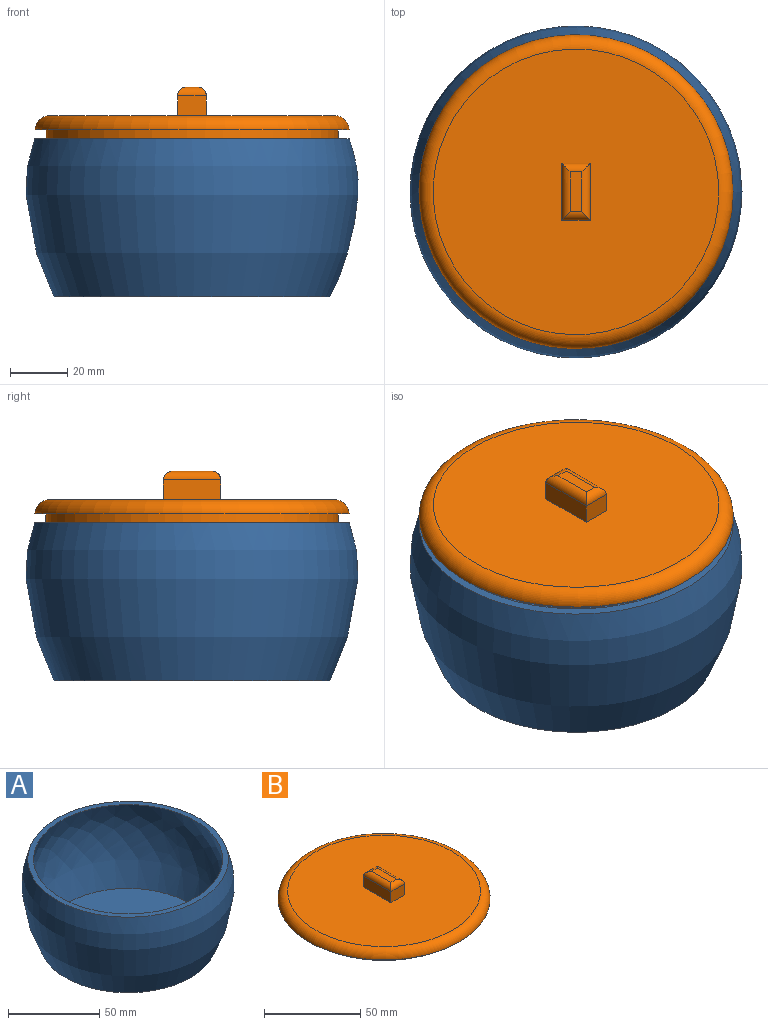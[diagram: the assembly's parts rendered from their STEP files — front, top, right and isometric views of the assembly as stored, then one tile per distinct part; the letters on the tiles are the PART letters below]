
ASSEMBLY  parts=2 mates=1
PART A: 5 faces, bbox 116.5x116.5x55.5 mm
  f0: plane 96.72x96.72mm, normal (0,0,-1), area 7347.7mm2, adj f1
  f1: revolved ~116.54x116.54mm, area 20018.4mm2, adj f0,f2
  f2: plane 110.14x110.14mm, normal (0,0,1), area 1062.9mm2, adj f1,f3
  f3: revolved ~110.54x110.54mm, area 17976.9mm2, adj f2,f4
  f4: plane 93.06x93.06mm, normal (0,0,1), area 6801.2mm2, adj f3
PART B: 14 faces, bbox 119.2x119.2x18 mm
  f0: cylinder r=51.25mm len=102.5mm, axis (0,0,1), area 966mm2, adj f1,f3
  f1: plane 102.5x102.5mm, normal (0,0,-1), area 8251.6mm2, adj f0
  f2: plane 100.14x100.14mm, normal (0,0,1), area 7675.5mm2, adj f4,f5,f6,f7,f8
  f3: plane 110.14x110.14mm, normal (0,0,-1), area 1275.3mm2, adj f0,f4
  f4: torus R=50.07mm, axis (0,0,1), area 2627.9mm2, adj f2,f3
  f5: plane 20x7mm, normal (1,0,0), area 140mm2, adj f2,f6,f8,f10
  f6: plane 10x7mm, normal (0,1,0), area 70mm2, adj f2,f5,f7,f11
  f7: plane 20x7mm, normal (-1,0,0), area 140mm2, adj f2,f6,f8,f13
  f8: plane 10x7mm, normal (0,-1,0), area 70mm2, adj f2,f5,f7,f12
  f9: plane 14x4mm, normal (0,0,1), area 56mm2, adj f10,f11,f12,f13
  f10: cylinder r=3mm len=20mm, axis (0,-1,0), area 84mm2, adj f5,f9,f11,f12
  f11: cylinder r=3mm len=10mm, axis (1,0,0), area 36.8mm2, adj f6,f9,f10,f13
  f12: cylinder r=3mm len=10mm, axis (-1,0,0), area 36.8mm2, adj f8,f9,f10,f13
  f13: cylinder r=3mm len=20mm, axis (0,1,0), area 84mm2, adj f7,f9,f11,f12
PLACE A t=(-1.46,6.73,10)mm fixed
PLACE B t=(-1.46,6.73,13)mm
MATE slider B.f0 <-> A.f2  axis (0,0,-1) through (-1.46,6.73,65.47)mm
